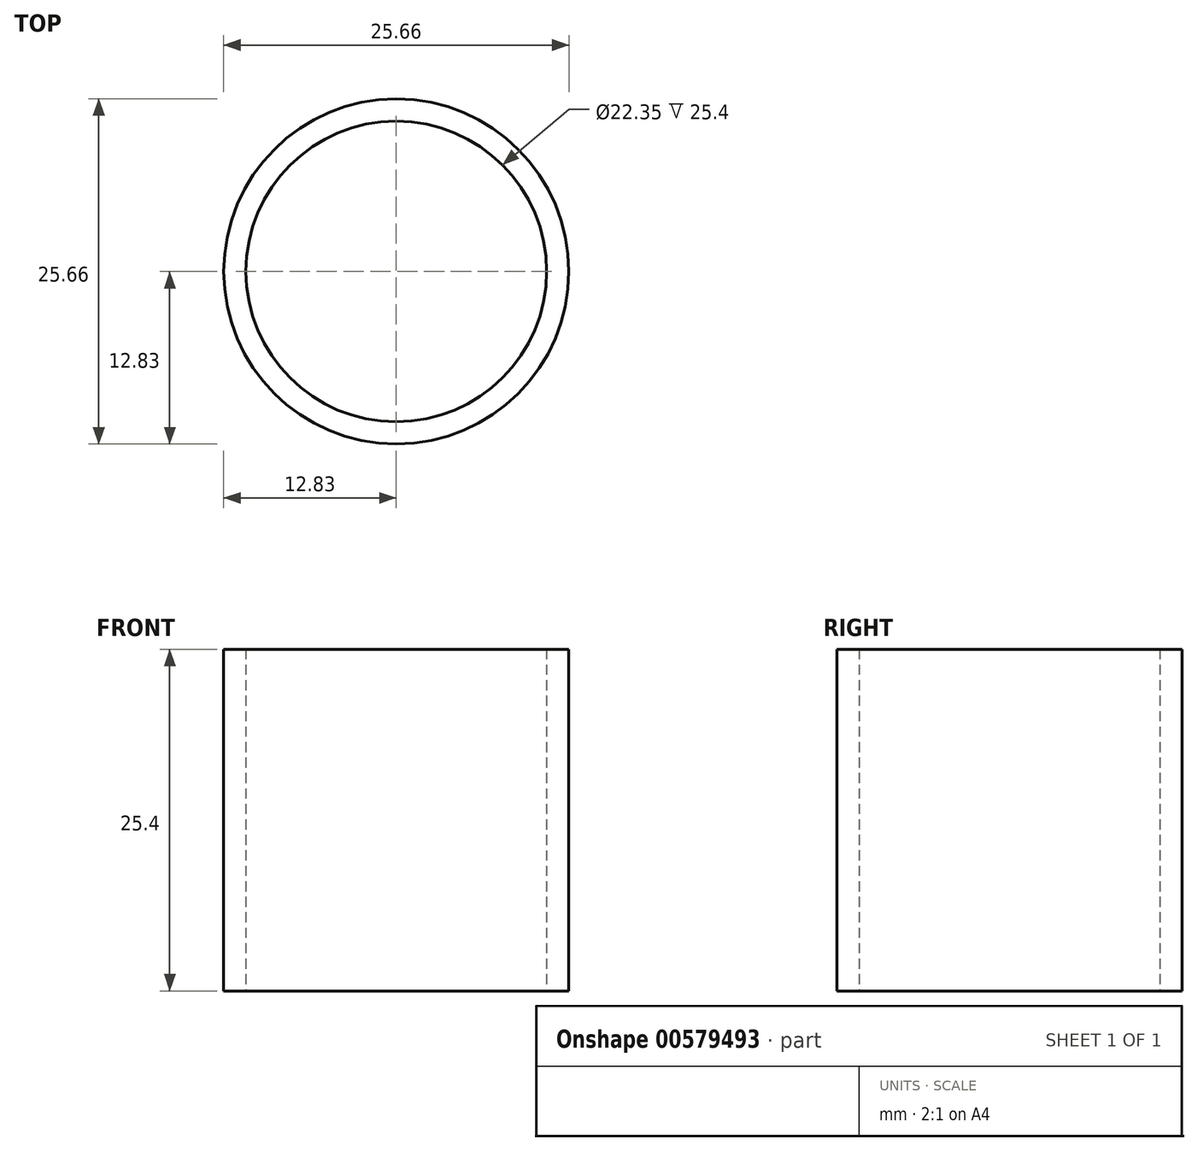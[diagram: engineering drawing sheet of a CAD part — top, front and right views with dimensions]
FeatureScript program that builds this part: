
annotation { "Feature Type Name" : "Feature", "Feature Type Description" : "" }
export const myFeature = defineFeature(function(context is Context, id is Id, definition is map)
    precondition{}
    {
        {
            var Q0;
            Q0=qCreatedBy(makeId("Top.planeOp"),FACE);
            var sketch = newSketch(context, id + "F0", { "sketchPlane" : qUnion([Q0])});
            skCircle(sketch, "E0", {"center": v(0, 0) * mm, "radius": 11.18 * mm});
            skCircle(sketch, "E1", {"center": v(0, 0) * mm, "radius": 12.83 * mm});
            skSolve(sketch);
        }
        {
            var Q0;
            Q0=makeQuery(id+"F0.imprint","IMPRINT",FACE,{"disambiguationData":[TD([[makeQuery(id+"F0.imprint","IMPRINT",EDGE,{"derivedFrom":sQuery(id+"F0.wireOp",EDGE,"E0")}),-1.0]])]});
            extrude(context, id + "F1", {"entities" : qUnion([Q0]), "depth" : 25.4 * mm, "offsetDistance" : 25.4 * mm});
        }
    });
